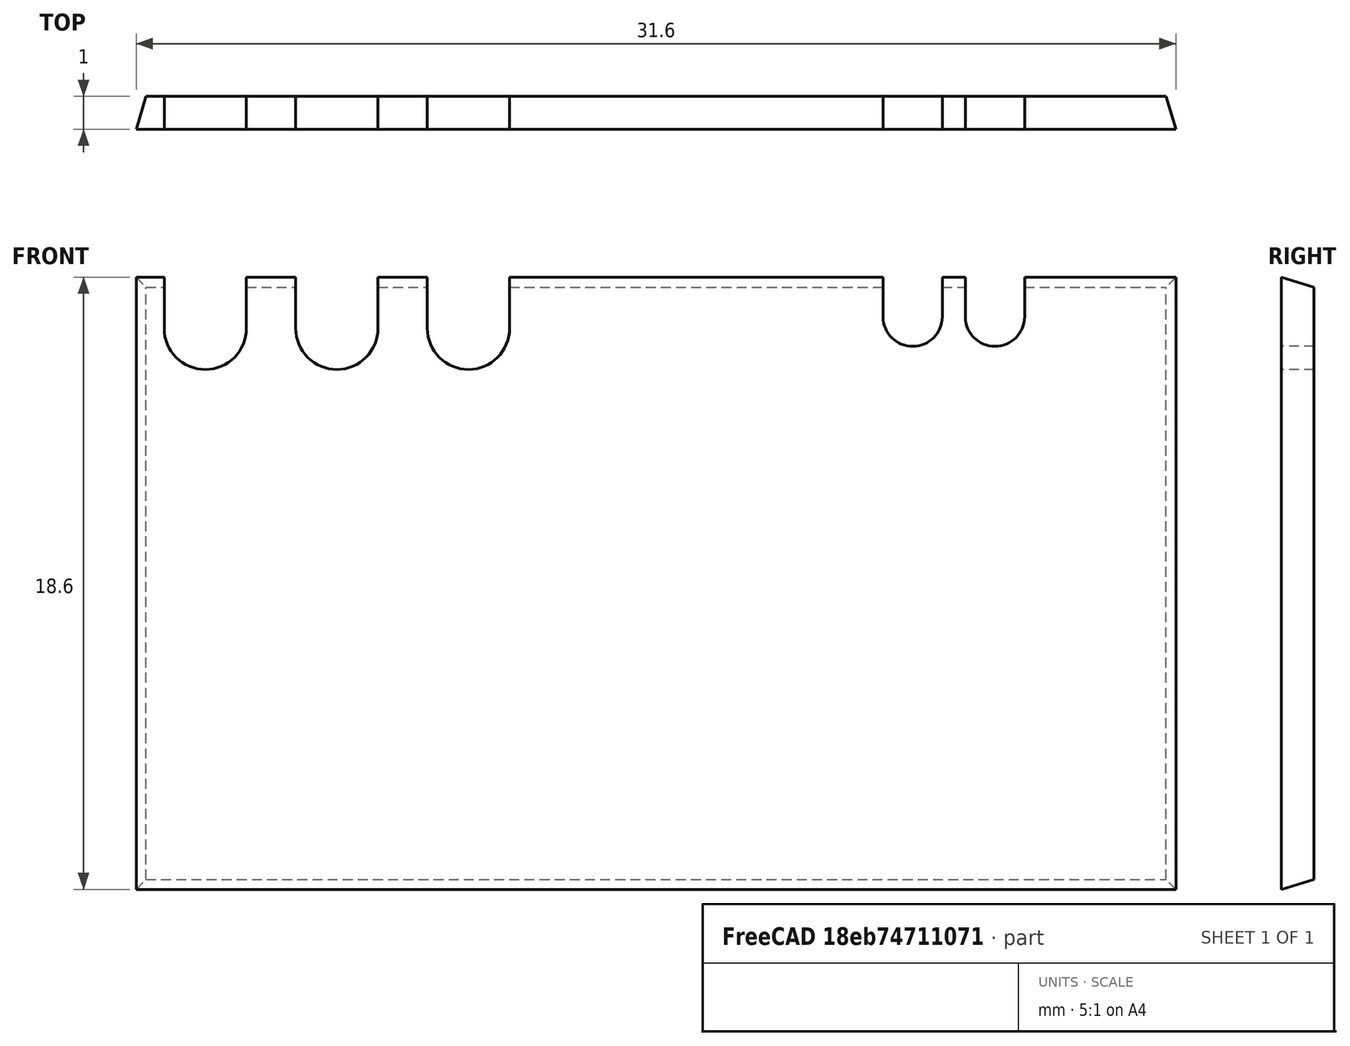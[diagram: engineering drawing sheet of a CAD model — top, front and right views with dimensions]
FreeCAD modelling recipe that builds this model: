
FCSTD DOCUMENT  (FreeCAD 0.20R29410 (Git))
Label: tapa
License: All rights reserved
LicenseURL: http://en.wikipedia.org/wiki/All_rights_reserved
objects: Part::Box×5, Part::Cylinder×5, Part::MultiFuse×1, Part::Wedge×1, Part::Cut×1
note: 13 computed .brp shape members not serialized (recipe doc carries the construction recipe); baked Part::Feature solids carry a one-line shape summary decoded from their .brp

FEATURE [Part::Box] Box022  label="Cubo002"
  AttacherType = Attacher::AttachEngine3D
  Height = 4
  Length = 2.5
  Placement = pos=(0.75,64,15.25) rot=(0,0,1;0rad)
  Width = 3
FEATURE [Part::Box] Box023  label="Cubo003"
  AttacherType = Attacher::AttachEngine3D
  Height = 4
  Length = 2.5
  Placement = pos=(4.75,64,15.25) rot=(0,0,1;0rad)
  Width = 3
FEATURE [Part::Box] Box024  label="Cubo004"
  AttacherType = Attacher::AttachEngine3D
  Height = 4
  Length = 2.5
  Placement = pos=(8.75,64,15.25) rot=(0,0,1;0rad)
  Width = 3
FEATURE [Part::Box] Box025  label="Cubo005"
  AttacherType = Attacher::AttachEngine3D
  Height = 4
  Length = 1.8
  Placement = pos=(22.6,64,15.6) rot=(0,0,1;0rad)
  Width = 3
FEATURE [Part::Box] Box026  label="Cubo006"
  AttacherType = Attacher::AttachEngine3D
  Height = 4
  Length = 1.8
  Placement = pos=(25.1,64,15.6) rot=(0,0,1;0rad)
  Width = 3
FEATURE [Part::Cylinder] Cylinder005  label="c003"
  Angle = 360
  AttacherType = Attacher::AttachEngine3D
  FirstAngle = 0
  Height = 76
  Placement = pos=(26,23,15.6) rot=(-1,0,0;1.5708rad)
  Radius = 0.9
  SecondAngle = 0
FEATURE [Part::Cylinder] Cylinder006  label="c004"
  Angle = 360
  AttacherType = Attacher::AttachEngine3D
  FirstAngle = 0
  Height = 76
  Placement = pos=(23.5,23,15.6) rot=(-1,0,0;1.5708rad)
  Radius = 0.9
  SecondAngle = 0
FEATURE [Part::Cylinder] Cylinder007  label="salida001"
  Angle = 360
  AttacherType = Attacher::AttachEngine3D
  FirstAngle = 0
  Height = 76
  Placement = pos=(10,23,15.25) rot=(-1,0,0;1.5708rad)
  Radius = 1.25
  SecondAngle = 0
FEATURE [Part::Cylinder] Cylinder008  label="neutro001"
  Angle = 360
  AttacherType = Attacher::AttachEngine3D
  FirstAngle = 0
  Height = 76
  Placement = pos=(6,23,15.25) rot=(-1,0,0;1.5708rad)
  Radius = 1.25
  SecondAngle = 0
FEATURE [Part::Cylinder] Cylinder009  label="vivo001"
  Angle = 360
  AttacherType = Attacher::AttachEngine3D
  FirstAngle = 0
  Height = 76
  Placement = pos=(2,23,15.25) rot=(-1,0,0;1.5708rad)
  Radius = 1.25
  SecondAngle = 0
FEATURE [Part::MultiFuse] Fusion007
  Shapes = -> [Cylinder009,Box022,Box023,Box024,Box025,Box026,Cylinder005,Cylinder006,Cylinder007,Cylinder008]
FEATURE [Part::Wedge] Wedge  label="Cuña"
  AttacherType = Attacher::AttachEngine3D
  Placement = pos=(-0.1,64.5,-1.8) rot=(0,0,1;0rad)
  X2max = 31.3
  X2min = 0.3
  Xmax = 31.6
  Xmin = 0
  Ymax = 1
  Ymin = 0
  Z2max = 18.3
  Z2min = 0.3
  Zmax = 18.6
  Zmin = 0
FEATURE [Part::Cut] Cut013  label="tapa"
  Base = -> Wedge
  Tool = -> Fusion007
